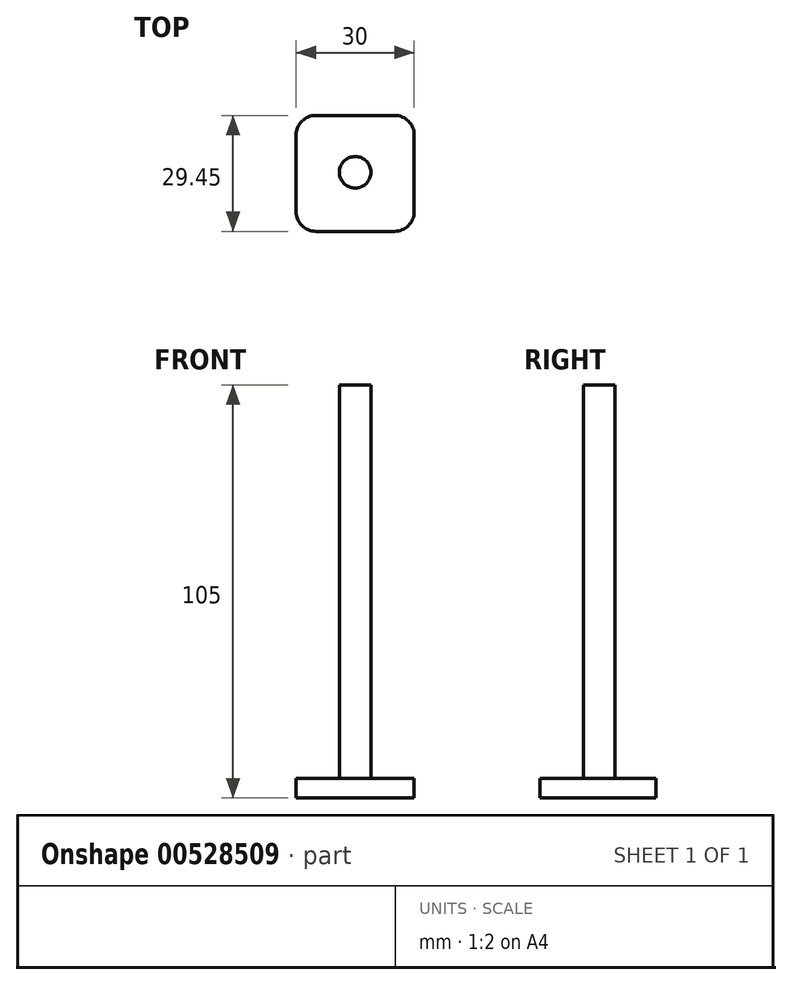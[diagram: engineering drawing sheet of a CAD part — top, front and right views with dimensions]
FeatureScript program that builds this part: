
annotation { "Feature Type Name" : "Feature", "Feature Type Description" : "" }
export const myFeature = defineFeature(function(context is Context, id is Id, definition is map)
    precondition{}
    {
        {
            var Q0;
            Q0=qCreatedBy(makeId("Top.planeOp"),FACE);
            var sketch = newSketch(context, id + "F0", { "sketchPlane" : qUnion([Q0])});
            skLineSegment(sketch, "E0.bottom", {"start": v(-10, 14.45) * mm, "end": v(10, 14.45) * mm});
            skLineSegment(sketch, "E0.top", {"start": v(-10, -15) * mm, "end": v(10, -15) * mm});
            skLineSegment(sketch, "E0.left", {"start": v(-15, 9.45) * mm, "end": v(-15, -10) * mm});
            skLineSegment(sketch, "E0.right", {"start": v(15, 9.45) * mm, "end": v(15, -10) * mm});
            skPoint(sketch, "E1.visualSharp", {"position": v(-15, 14.45) * mm});
            skArc(sketch, "E1.filletArc", {"start": v(-10, 14.45) * mm, "mid": v(-13.54, 12.98) * mm, "end": v(-15, 9.45) * mm});
            skPoint(sketch, "E2.visualSharp", {"position": v(15, 14.45) * mm});
            skArc(sketch, "E2.filletArc", {"start": v(15, 9.45) * mm, "mid": v(13.54, 12.98) * mm, "end": v(10, 14.45) * mm});
            skPoint(sketch, "E3.visualSharp", {"position": v(15, -15) * mm});
            skArc(sketch, "E3.filletArc", {"start": v(10, -15) * mm, "mid": v(13.54, -13.54) * mm, "end": v(15, -10) * mm});
            skPoint(sketch, "E4.visualSharp", {"position": v(-15, -15) * mm});
            skArc(sketch, "E4.filletArc", {"start": v(-15, -10) * mm, "mid": v(-13.54, -13.54) * mm, "end": v(-10, -15) * mm});
            skSolve(sketch);
        }
        {
            var Q0;
            Q0 = qSketchRegion(id + "F0", true);
            extrude(context, id + "F1", {"entities" : qUnion([Q0]), "depth" : 5 * mm, "offsetDistance" : 25 * mm});
        }
        {
            var Q0;
            Q0=makeQuery(id+"F1.opExtrude","CAP_FACE",FACE,{"disambiguationData":[OSD([sQuery(id+"F0.wireOp",EDGE,"E0.bottom"),sQuery(id+"F0.wireOp",EDGE,"E0.top"),sQuery(id+"F0.wireOp",EDGE,"E0.left"),sQuery(id+"F0.wireOp",EDGE,"E0.right"),sQuery(id+"F0.wireOp",EDGE,"E1.filletArc"),sQuery(id+"F0.wireOp",EDGE,"E2.filletArc"),sQuery(id+"F0.wireOp",EDGE,"E3.filletArc"),sQuery(id+"F0.wireOp",EDGE,"E4.filletArc")])],"isStart":false});
            var sketch = newSketch(context, id + "F2", { "sketchPlane" : qUnion([Q0])});
            skCircle(sketch, "E5", {"center": v(0, 0) * mm, "radius": 4 * mm});
            skSolve(sketch);
        }
        {
            var Q0;
            Q0=makeQuery(id+"F2.imprint","IMPRINT",FACE,{"disambiguationData":[TD([[makeQuery(id+"F2.imprint","IMPRINT",EDGE,{"derivedFrom":sQuery(id+"F2.wireOp",EDGE,"E5")}),1.0]])]});
            extrude(context, id + "F3", {"entities" : qUnion([Q0]), "operationType" : NewBodyOperationType.ADD, "depth" : 100 * mm, "offsetDistance" : 25 * mm});
        }
    });
